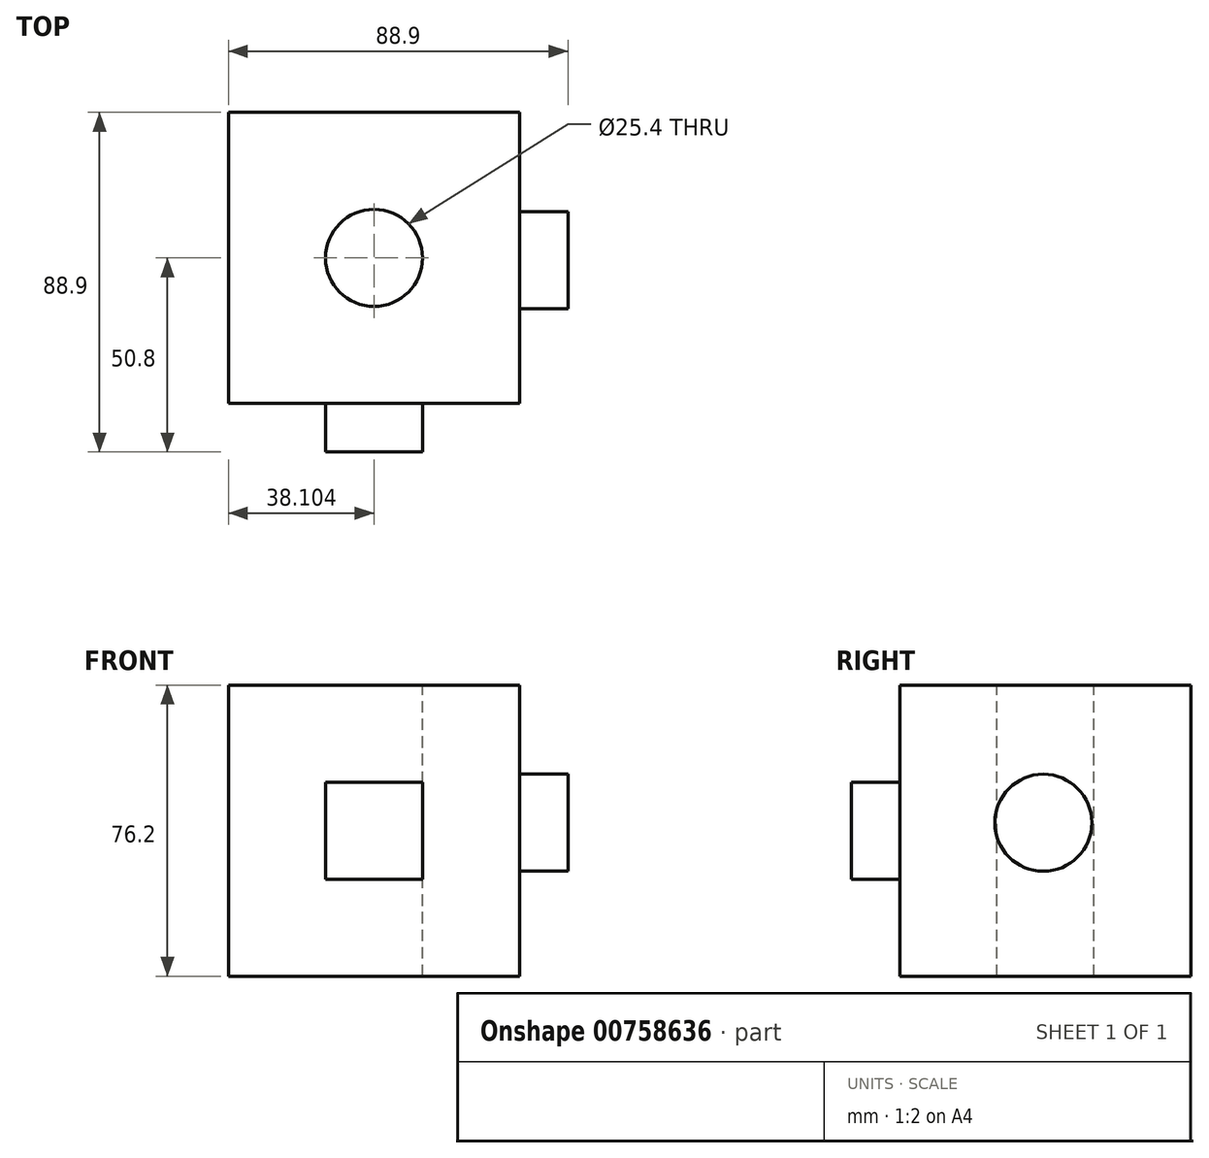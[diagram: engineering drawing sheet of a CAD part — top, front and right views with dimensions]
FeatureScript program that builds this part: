
annotation { "Feature Type Name" : "Feature", "Feature Type Description" : "" }
export const myFeature = defineFeature(function(context is Context, id is Id, definition is map)
    precondition{}
    {
        {
            var Q0;
            Q0=qCreatedBy(makeId("Front.planeOp"),FACE);
            var sketch = newSketch(context, id + "F0", { "sketchPlane" : qUnion([Q0])});
            skLineSegment(sketch, "E0.bottom", {"start": v(-70.08, 36.05) * mm, "end": v(6.12, 36.05) * mm});
            skLineSegment(sketch, "E0.top", {"start": v(-70.08, -40.15) * mm, "end": v(6.12, -40.15) * mm});
            skLineSegment(sketch, "E0.left", {"start": v(-70.08, 36.05) * mm, "end": v(-70.08, -40.15) * mm});
            skLineSegment(sketch, "E0.right", {"start": v(6.12, 36.05) * mm, "end": v(6.12, -40.15) * mm});
            skSolve(sketch);
        }
        {
            var Q0;
            Q0=makeQuery(id+"F0.imprint","IMPRINT",FACE,{"disambiguationData":[TD([[makeQuery(id+"F0.imprint","IMPRINT",EDGE,{"derivedFrom":sQuery(id+"F0.wireOp",EDGE,"E0.bottom")}),-1.0]])]});
            extrude(context, id + "F1", {"entities" : qUnion([Q0]), "depth" : 76.2 * mm, "offsetDistance" : 25.4 * mm});
        }
        {
            var Q0;
            Q0=makeQuery(id+"F1.opExtrude","CAP_FACE",FACE,{"disambiguationData":[OSD([sQuery(id+"F0.wireOp",EDGE,"E0.bottom"),sQuery(id+"F0.wireOp",EDGE,"E0.top"),sQuery(id+"F0.wireOp",EDGE,"E0.left"),sQuery(id+"F0.wireOp",EDGE,"E0.right")])],"isStart":false});
            var sketch = newSketch(context, id + "F2", { "sketchPlane" : qUnion([Q0])});
            skLineSegment(sketch, "E1.bottom", {"start": v(-44.68, 10.65) * mm, "end": v(-19.28, 10.65) * mm});
            skLineSegment(sketch, "E1.top", {"start": v(-44.68, -14.75) * mm, "end": v(-19.28, -14.75) * mm});
            skLineSegment(sketch, "E1.left", {"start": v(-44.68, 10.65) * mm, "end": v(-44.68, -14.75) * mm});
            skLineSegment(sketch, "E1.right", {"start": v(-19.28, 10.65) * mm, "end": v(-19.28, -14.75) * mm});
            skSolve(sketch);
        }
        {
            var Q0;
            Q0=makeQuery(id+"F2.imprint","IMPRINT",FACE,{"disambiguationData":[TD([[makeQuery(id+"F2.imprint","IMPRINT",EDGE,{"derivedFrom":sQuery(id+"F2.wireOp",EDGE,"E1.bottom")}),-1.0]])]});
            extrude(context, id + "F3", {"entities" : qUnion([Q0]), "operationType" : NewBodyOperationType.ADD, "depth" : 12.7 * mm, "offsetDistance" : 25.4 * mm});
        }
        {
            var Q0;
            Q0=makeQuery(id+"F1.opExtrude","SWEPT_FACE",FACE,{"disambiguationData":[OSD([sQuery(id+"F0.wireOp",EDGE,"E0.bottom")])]});
            var sketch = newSketch(context, id + "F4", { "sketchPlane" : qUnion([Q0])});
            skPoint(sketch, "E2", {"position": v(-31.98, -38.1) * mm});
            skSolve(sketch);
        }
        {
            var Q0;
            Q0=sQuery(id+"F4.wireOp",VERTEX,"E2");
            var Q1;
            Q1=makeQuery(id+"F1.opExtrude","SWEPT_BODY",BODY,{"disambiguationData":[OSD([sQuery(id+"F0.wireOp",EDGE,"E0.bottom"),sQuery(id+"F0.wireOp",EDGE,"E0.top"),sQuery(id+"F0.wireOp",EDGE,"E0.left"),sQuery(id+"F0.wireOp",EDGE,"E0.right")])]});
            hole(context, id + "F5", {"style" : HoleStyle.SIMPLE, "endStyle" : HoleEndStyle.THROUGH, "holeDiameter" : 25.4 * mm, "majorDiameter" : 6.35 * mm, "isTappedThrough" : true, "tappedDepth" : 12.7 * mm, "tapClearance" : 3, "locations" : qUnion([Q0]), "scope" : qUnion([Q1])});
        }
        {
            var Q0;
            Q0=makeQuery(id+"F1.opExtrude","SWEPT_FACE",FACE,{"disambiguationData":[OSD([sQuery(id+"F0.wireOp",EDGE,"E0.right")])]});
            var sketch = newSketch(context, id + "F6", { "sketchPlane" : qUnion([Q0])});
            skCircle(sketch, "E3", {"center": v(-38.66, 0) * mm, "radius": 12.7 * mm});
            skSolve(sketch);
        }
        {
            var Q0;
            Q0=makeQuery(id+"F6.imprint","IMPRINT",FACE,{"disambiguationData":[TD([[makeQuery(id+"F6.imprint","IMPRINT",EDGE,{"derivedFrom":sQuery(id+"F6.wireOp",EDGE,"E3")}),1.0]])]});
            extrude(context, id + "F7", {"entities" : qUnion([Q0]), "operationType" : NewBodyOperationType.ADD, "depth" : 12.7 * mm, "offsetDistance" : 25.4 * mm});
        }
    });
